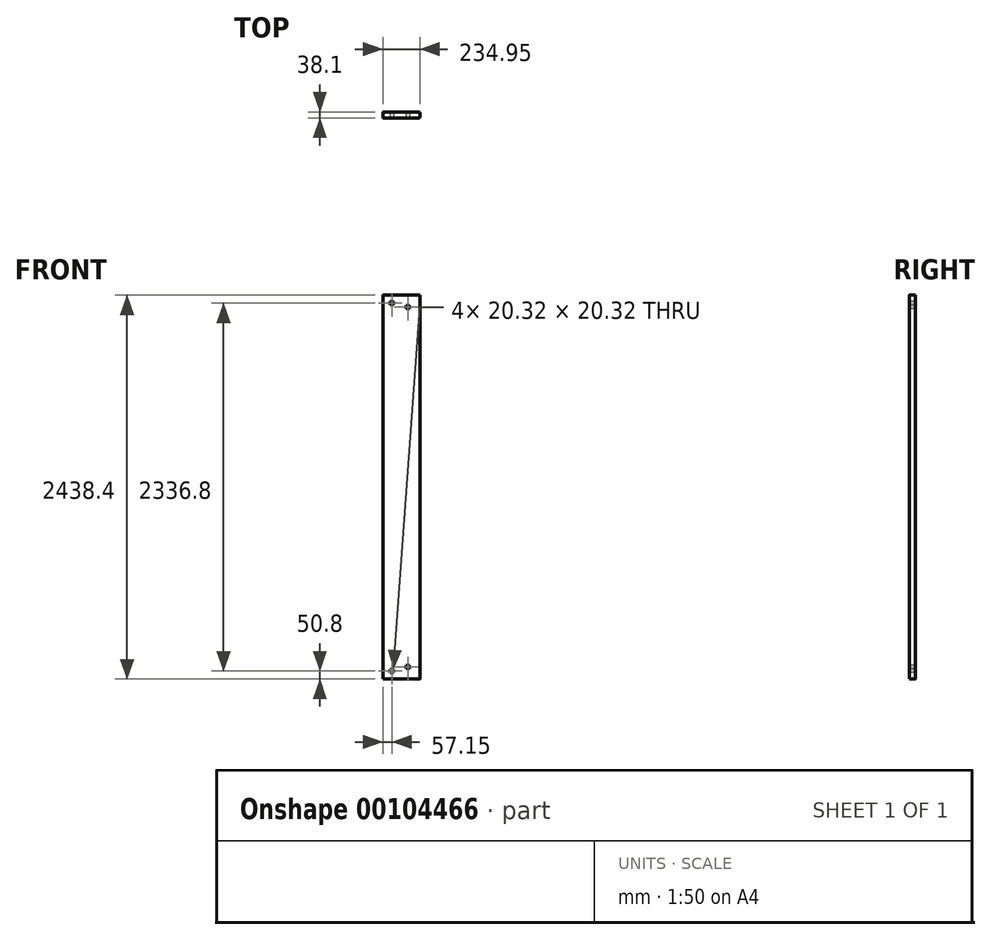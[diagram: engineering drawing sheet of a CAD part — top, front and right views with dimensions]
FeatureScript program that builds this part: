
annotation { "Feature Type Name" : "Feature", "Feature Type Description" : "" }
export const myFeature = defineFeature(function(context is Context, id is Id, definition is map)
    precondition{}
    {
        {
            var Q0;
            Q0=qCreatedBy(makeId("Top.planeOp"),FACE);
            var sketch = newSketch(context, id + "F0", { "sketchPlane" : qUnion([Q0])});
            skLineSegment(sketch, "E0.bottom", {"start": v(0, 0) * mm, "end": v(234.95, 0) * mm});
            skLineSegment(sketch, "E0.top", {"start": v(0, 38.1) * mm, "end": v(234.95, 38.1) * mm});
            skLineSegment(sketch, "E0.left", {"start": v(0, 0) * mm, "end": v(0, 38.1) * mm});
            skLineSegment(sketch, "E0.right", {"start": v(234.95, 0) * mm, "end": v(234.95, 38.1) * mm});
            skSolve(sketch);
        }
        {
            var Q0;
            Q0=makeQuery(id+"F0.imprint","IMPRINT",FACE,{"disambiguationData":[TD([[makeQuery(id+"F0.imprint","IMPRINT",EDGE,{"derivedFrom":sQuery(id+"F0.wireOp",EDGE,"E0.bottom")}),1.0]])]});
            extrude(context, id + "F1", {"entities" : qUnion([Q0]), "depth" : 2438.4 * mm});
        }
        {
            var Q0;
            Q0=makeQuery(id+"F1.opExtrude","SWEPT_FACE",FACE,{"disambiguationData":[OSD([sQuery(id+"F0.wireOp",EDGE,"E0.bottom")])]});
            var sketch = newSketch(context, id + "F2", { "sketchPlane" : qUnion([Q0])});
            skLineSegment(sketch, "E1.bottom", {"start": v(67.3, 2397.76) * mm, "end": v(46.99, 2397.76) * mm});
            skLineSegment(sketch, "E1.top", {"start": v(67.3, 2377.44) * mm, "end": v(46.99, 2377.44) * mm});
            skLineSegment(sketch, "E1.left", {"start": v(67.3, 2397.76) * mm, "end": v(67.3, 2377.44) * mm});
            skLineSegment(sketch, "E1.right", {"start": v(46.99, 2397.76) * mm, "end": v(46.99, 2377.44) * mm});
            skPoint(sketch, "E1.middle", {"position": v(57.15, 2387.6) * mm});
            skLineSegment(sketch, "E2.bottom", {"start": v(168.9, 2372.36) * mm, "end": v(148.6, 2372.36) * mm});
            skLineSegment(sketch, "E2.top", {"start": v(168.9, 2352.04) * mm, "end": v(148.6, 2352.04) * mm});
            skLineSegment(sketch, "E2.left", {"start": v(168.9, 2372.36) * mm, "end": v(168.9, 2352.04) * mm});
            skLineSegment(sketch, "E2.right", {"start": v(148.6, 2372.36) * mm, "end": v(148.6, 2352.04) * mm});
            skPoint(sketch, "E2.middle", {"position": v(158.75, 2362.2) * mm});
            skLineSegment(sketch, "E3", {"start": v(0, 1219.2) * mm, "end": v(234.95, 1219.2) * mm, "construction": true});
            skLineSegment(sketch, "E4.MirrorCS", {"start": v(148.6, 66.04) * mm, "end": v(148.6, 86.36) * mm});
            skLineSegment(sketch, "E5.MirrorCS", {"start": v(67.31, 40.64) * mm, "end": v(47, 40.64) * mm});
            skLineSegment(sketch, "E6.MirrorCS", {"start": v(168.9, 66.04) * mm, "end": v(168.9, 86.36) * mm});
            skLineSegment(sketch, "E7.MirrorCS", {"start": v(168.91, 86.36) * mm, "end": v(148.6, 86.36) * mm});
            skLineSegment(sketch, "E8.MirrorCS", {"start": v(67.31, 60.96) * mm, "end": v(47, 60.96) * mm});
            skLineSegment(sketch, "E9.MirrorCS", {"start": v(168.91, 66.04) * mm, "end": v(148.6, 66.04) * mm});
            skLineSegment(sketch, "E10.MirrorCS", {"start": v(46.99, 40.64) * mm, "end": v(46.99, 60.96) * mm});
            skLineSegment(sketch, "E11.MirrorCS", {"start": v(67.31, 40.64) * mm, "end": v(67.31, 60.96) * mm});
            skPoint(sketch, "E12.MirrorP", {"position": v(158.75, 76.2) * mm});
            skPoint(sketch, "E13.MirrorP", {"position": v(57.15, 50.8) * mm});
            skSolve(sketch);
        }
        {
            var Q0;
            Q0=makeQuery(id+"F2.imprint","IMPRINT",FACE,{"disambiguationData":[TD([[makeQuery(id+"F2.imprint","IMPRINT",EDGE,{"derivedFrom":sQuery(id+"F2.wireOp",EDGE,"E1.bottom")}),1.0]])]});
            var Q1;
            Q1=makeQuery(id+"F2.imprint","IMPRINT",FACE,{"disambiguationData":[TD([[makeQuery(id+"F2.imprint","IMPRINT",EDGE,{"derivedFrom":sQuery(id+"F2.wireOp",EDGE,"E2.bottom")}),1.0]])]});
            var Q2;
            Q2=makeQuery(id+"F2.imprint","IMPRINT",FACE,{"disambiguationData":[TD([[makeQuery(id+"F2.imprint","IMPRINT",EDGE,{"derivedFrom":sQuery(id+"F2.wireOp",EDGE,"E4.MirrorCS")}),-1.0]])]});
            var Q3;
            Q3=makeQuery(id+"F2.imprint","IMPRINT",FACE,{"disambiguationData":[TD([[makeQuery(id+"F2.imprint","IMPRINT",EDGE,{"derivedFrom":sQuery(id+"F2.wireOp",EDGE,"E5.MirrorCS")}),-1.0]])]});
            extrude(context, id + "F3", {"entities" : qUnion([Q0, Q1, Q2, Q3]), "operationType" : NewBodyOperationType.REMOVE, "oppositeDirection" : true, "depth" : 50.8 * mm});
        }
        {
            var Q0;
            Q0=makeQuery(id+"F1.opExtrude","SWEPT_EDGE",EDGE,{"disambiguationData":[OSD([sQuery(id+"F0.wireOp",EDGE,"E0.bottom"),sQuery(id+"F0.wireOp",EDGE,"E0.left")])]});
            var Q1;
            Q1=makeQuery(id+"F1.opExtrude","SWEPT_EDGE",EDGE,{"disambiguationData":[OSD([sQuery(id+"F0.wireOp",EDGE,"E0.bottom"),sQuery(id+"F0.wireOp",EDGE,"E0.right")])]});
            var Q2;
            Q2=makeQuery(id+"F1.opExtrude","SWEPT_EDGE",EDGE,{"disambiguationData":[OSD([sQuery(id+"F0.wireOp",EDGE,"E0.top"),sQuery(id+"F0.wireOp",EDGE,"E0.left")])]});
            var Q3;
            Q3=makeQuery(id+"F1.opExtrude","SWEPT_EDGE",EDGE,{"disambiguationData":[OSD([sQuery(id+"F0.wireOp",EDGE,"E0.top"),sQuery(id+"F0.wireOp",EDGE,"E0.right")])]});
            fillet(context, id + "F4", {"entities" : qUnion([Q0, Q1, Q2, Q3]), "radius" : 5.08 * mm, "tangentPropagation" : true, "allowEdgeOverflow" : false});
        }
    });
